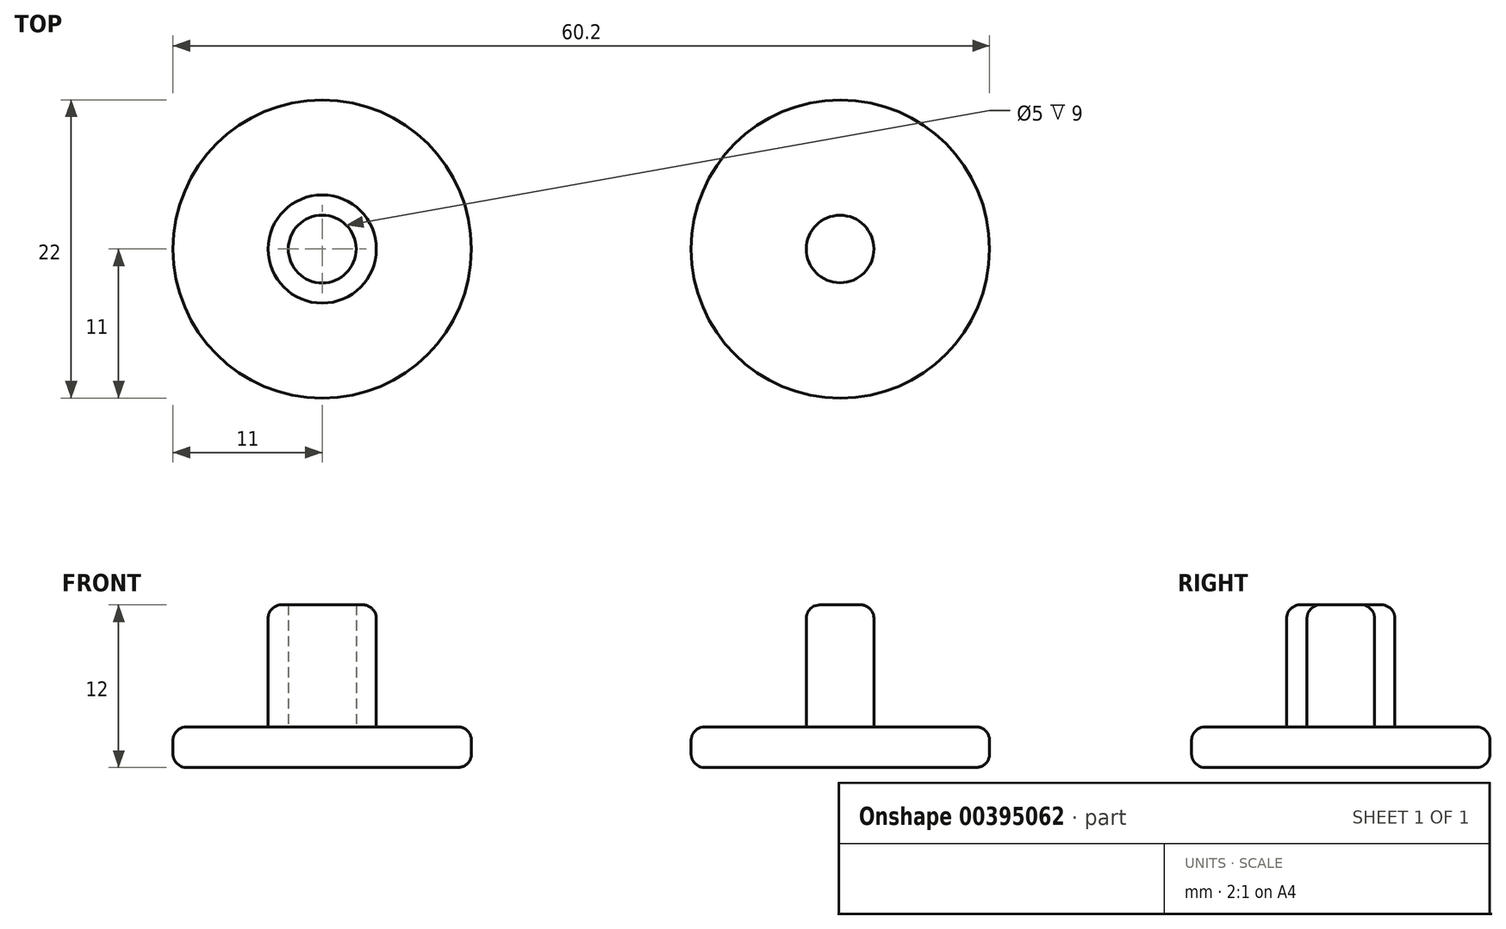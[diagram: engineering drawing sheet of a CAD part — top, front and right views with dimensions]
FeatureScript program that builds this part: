
annotation { "Feature Type Name" : "Feature", "Feature Type Description" : "" }
export const myFeature = defineFeature(function(context is Context, id is Id, definition is map)
    precondition{}
    {
        {
            var Q0;
            Q0=qCreatedBy(makeId("Top.planeOp"),FACE);
            var sketch = newSketch(context, id + "F0", { "sketchPlane" : qUnion([Q0])});
            skCircle(sketch, "E0", {"center": v(0, 0) * mm, "radius": 11 * mm});
            skCircle(sketch, "E1", {"center": v(38.2, 0) * mm, "radius": 11 * mm});
            skSolve(sketch);
        }
        {
            var Q0;
            Q0=makeQuery(id+"F0.imprint","IMPRINT",FACE,{"disambiguationData":[TD([[makeQuery(id+"F0.imprint","IMPRINT",EDGE,{"derivedFrom":sQuery(id+"F0.wireOp",EDGE,"E1")}),1.0]])]});
            var Q1;
            Q1=makeQuery(id+"F0.imprint","IMPRINT",FACE,{"disambiguationData":[TD([[makeQuery(id+"F0.imprint","IMPRINT",EDGE,{"derivedFrom":sQuery(id+"F0.wireOp",EDGE,"E0")}),1.0]])]});
            extrude(context, id + "F1", {"entities" : qUnion([Q0, Q1]), "depth" : 3 * mm});
        }
        {
            var Q0;
            Q0=makeQuery(id+"F1.opExtrude","CAP_FACE",FACE,{"disambiguationData":[OSD([sQuery(id+"F0.wireOp",EDGE,"E0")])],"isStart":false});
            var Q1;
            Q1=makeQuery(id+"F1.opExtrude","CAP_FACE",FACE,{"disambiguationData":[OSD([sQuery(id+"F0.wireOp",EDGE,"E1")])],"isStart":false});
            cPlane(context, id + "F2", {"entities" : qUnion([Q0, Q1]), "cplaneType" : CPlaneType.MID_PLANE, "offset" : 25 * mm, "width" : 150 * mm, "height" : 150 * mm});
        }
        {
            var Q0;
            Q0=qCreatedBy(id+"F2.planeOp",FACE);
            var sketch = newSketch(context, id + "F3", { "sketchPlane" : qUnion([Q0])});
            skCircle(sketch, "E2", {"center": v(0, 0) * mm, "radius": 2.5 * mm});
            skCircle(sketch, "E3", {"center": v(0, 0) * mm, "radius": 4 * mm});
            skCircle(sketch, "E4", {"center": v(38.18, 0) * mm, "radius": 2.5 * mm});
            skSolve(sketch);
        }
        {
            var Q0;
            Q0=makeQuery(id+"F3.imprint","IMPRINT",FACE,{"disambiguationData":[TD([[makeQuery(id+"F3.imprint","IMPRINT",EDGE,{"derivedFrom":sQuery(id+"F3.wireOp",EDGE,"E2")}),-1.0]])]});
            var Q1;
            Q1=makeQuery(id+"F3.imprint","IMPRINT",FACE,{"disambiguationData":[TD([[makeQuery(id+"F3.imprint","IMPRINT",EDGE,{"derivedFrom":sQuery(id+"F3.wireOp",EDGE,"E4")}),1.0]])]});
            extrude(context, id + "F4", {"entities" : qUnion([Q0, Q1]), "depth" : 9 * mm});
        }
        {
            var Q0;
            Q0=makeQuery(id+"F1.opExtrude","CAP_EDGE",EDGE,{"disambiguationData":[OSD([sQuery(id+"F0.wireOp",EDGE,"E0")])],"isStart":true});
            var Q1;
            Q1=makeQuery(id+"F1.opExtrude","CAP_EDGE",EDGE,{"disambiguationData":[OSD([sQuery(id+"F0.wireOp",EDGE,"E0")])],"isStart":false});
            var Q2;
            Q2=makeQuery(id+"F1.opExtrude","CAP_EDGE",EDGE,{"disambiguationData":[OSD([sQuery(id+"F0.wireOp",EDGE,"E1")])],"isStart":false});
            var Q3;
            Q3=makeQuery(id+"F1.opExtrude","SWEPT_FACE",FACE,{"disambiguationData":[OSD([sQuery(id+"F0.wireOp",EDGE,"E1")])]});
            var Q4;
            Q4=makeQuery(id+"F4.opExtrude","CAP_EDGE",EDGE,{"disambiguationData":[OSD([sQuery(id+"F3.wireOp",EDGE,"E3")])],"isStart":false});
            var Q5;
            Q5=makeQuery(id+"F4.opExtrude","CAP_EDGE",EDGE,{"disambiguationData":[OSD([sQuery(id+"F3.wireOp",EDGE,"E4")])],"isStart":false});
            fillet(context, id + "F5", {"entities" : qUnion([Q0, Q1, Q2, Q3, Q4, Q5]), "radius" : 1 * mm, "tangentPropagation" : true, "allowEdgeOverflow" : false});
        }
    });
